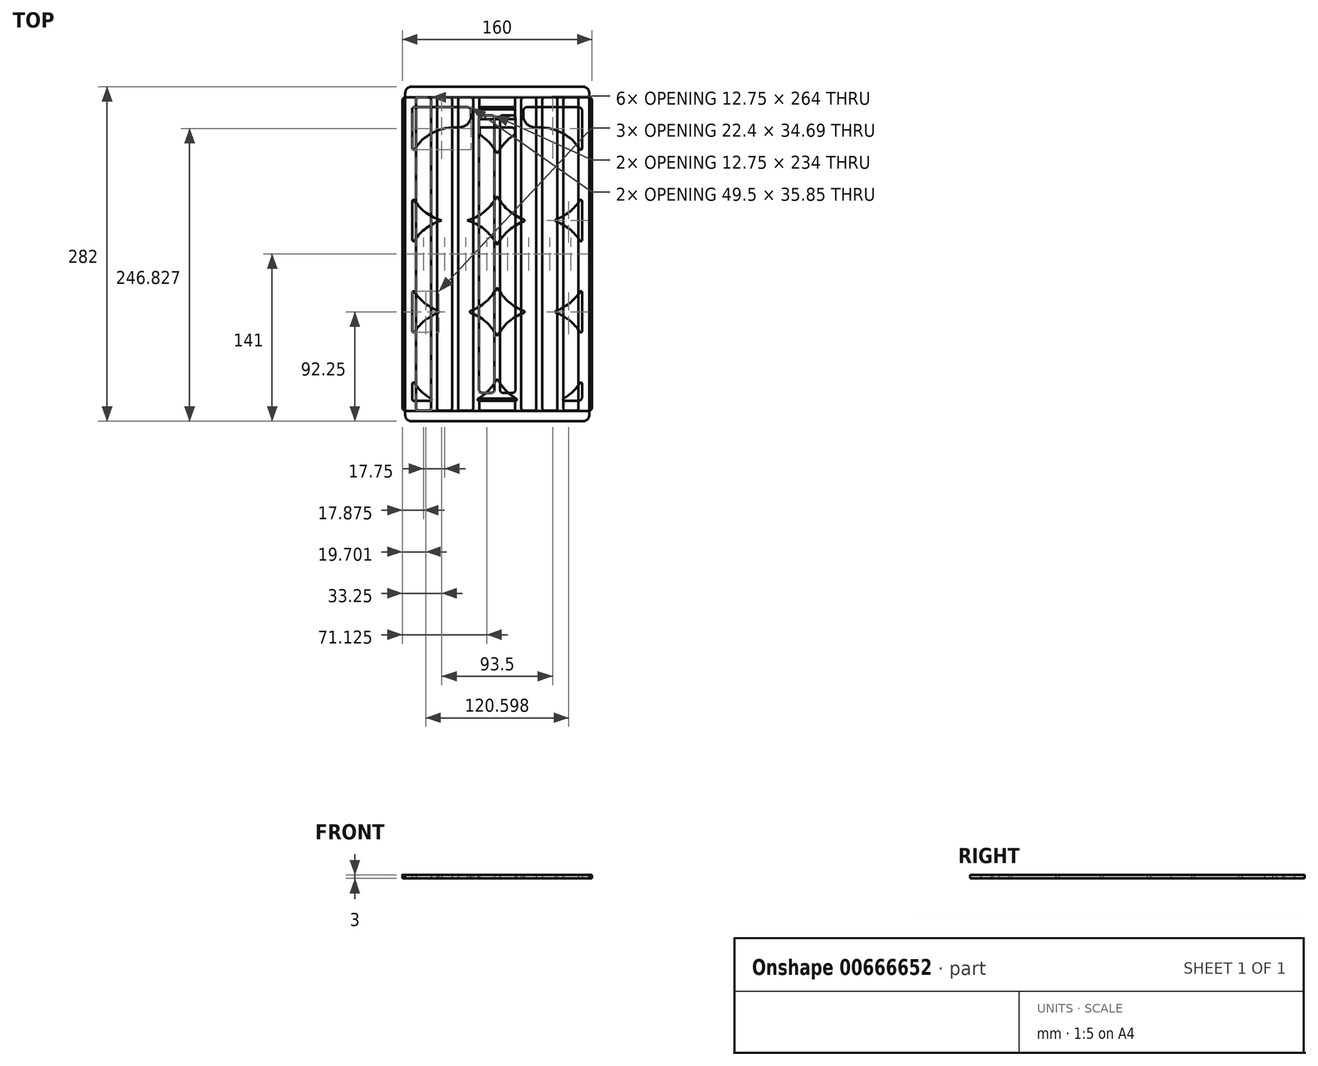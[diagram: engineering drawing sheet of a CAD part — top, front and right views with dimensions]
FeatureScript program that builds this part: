
annotation { "Feature Type Name" : "Feature", "Feature Type Description" : "" }
export const myFeature = defineFeature(function(context is Context, id is Id, definition is map)
    precondition{}
    {
        {
            var Q0;
            Q0=qCreatedBy(makeId("Top.planeOp"),FACE);
            var sketch = newSketch(context, id + "F0", { "sketchPlane" : qUnion([Q0])});
            skLineSegment(sketch, "E0.bottom", {"start": v(-80, 132.25) * mm, "end": v(80, 132.25) * mm});
            skLineSegment(sketch, "E0.top", {"start": v(-80, -132.25) * mm, "end": v(80, -132.25) * mm});
            skLineSegment(sketch, "E0.left", {"start": v(-80, 132.25) * mm, "end": v(-80, -132.25) * mm});
            skLineSegment(sketch, "E0.right", {"start": v(80, 132.25) * mm, "end": v(80, -132.25) * mm});
            skLineSegment(sketch, "E1.0", {"start": v(-71.5, 123.75) * mm, "end": v(-71.5, 85.18) * mm});
            skLineSegment(sketch, "E1.1", {"start": v(-71.5, 123.75) * mm, "end": v(-22, 123.75) * mm});
            skLineSegment(sketch, "E1.2", {"start": v(71.5, 123.75) * mm, "end": v(71.5, 85.18) * mm});
            skLineSegment(sketch, "E1.3", {"start": v(-71.5, -123.75) * mm, "end": v(-52.36, -123.75) * mm});
            skLineSegment(sketch, "E2.bottom", {"start": v(-15, 123.75) * mm, "end": v(15, 123.75) * mm});
            skLineSegment(sketch, "E2.top", {"start": v(-15, 113.75) * mm, "end": v(15, 113.75) * mm});
            skLineSegment(sketch, "E2.left", {"start": v(-15, 123.75) * mm, "end": v(-15, 113.75) * mm});
            skLineSegment(sketch, "E2.right", {"start": v(15, 123.75) * mm, "end": v(15, 113.75) * mm});
            skLineSegment(sketch, "E3", {"start": v(0, 0) * mm, "end": v(0, 132.25) * mm, "construction": true});
            skLineSegment(sketch, "E4", {"start": v(0, 0) * mm, "end": v(71.5, 0) * mm, "construction": true});
            skArc(sketch, "E5", {"start": v(-71.5, -105.68) * mm, "mid": v(-63.46, -116.34) * mm, "end": v(-52.36, -123.75) * mm});
            skArc(sketch, "E6", {"start": v(-71.5, 48.32) * mm, "mid": v(-61.25, 35.73) * mm, "end": v(-46.85, 28.25) * mm});
            skLineSegment(sketch, "E7", {"start": v(-36, -87.25) * mm, "end": v(-36, 66.75) * mm, "construction": true});
            skArc(sketch, "E8", {"start": v(-46.85, 28.25) * mm, "mid": v(-61.25, 20.77) * mm, "end": v(-71.5, 8.18) * mm});
            skArc(sketch, "E9.MirrorC", {"start": v(-25.15, -48.75) * mm, "mid": v(-10.32, -56.59) * mm, "end": v(0, -69.81) * mm});
            skArc(sketch, "E10.MirrorC", {"start": v(-25.15, 28.25) * mm, "mid": v(-10.32, 20.41) * mm, "end": v(0, 7.19) * mm});
            skArc(sketch, "E11.MirrorC", {"start": v(-71.5, 85.18) * mm, "mid": v(-56.77, 100.94) * mm, "end": v(-36, 106.75) * mm});
            skArc(sketch, "E12.MirrorC", {"start": v(0, 49.31) * mm, "mid": v(10.32, 36.09) * mm, "end": v(25.15, 28.25) * mm});
            skArc(sketch, "E13.MirrorC", {"start": v(71.5, -28.68) * mm, "mid": v(61.25, -41.27) * mm, "end": v(46.85, -48.75) * mm});
            skArc(sketch, "E14.MirrorC", {"start": v(52.36, -123.75) * mm, "mid": v(63.46, -116.34) * mm, "end": v(71.5, -105.68) * mm});
            skLineSegment(sketch, "E15.MirrorCS", {"start": v(36, -87.25) * mm, "end": v(36, 66.75) * mm, "construction": true});
            skLineSegment(sketch, "E16.0", {"start": v(22, 123.75) * mm, "end": v(22, 106.75) * mm});
            skLineSegment(sketch, "E16.1", {"start": v(-14.66, 106.75) * mm, "end": v(15.03, 106.75) * mm});
            skLineSegment(sketch, "E16.2", {"start": v(-22, 123.75) * mm, "end": v(-22, 106.75) * mm});
            skLineSegment(sketch, "E17", {"start": v(-22, 106.75) * mm, "end": v(-36, 106.75) * mm});
            skLineSegment(sketch, "E18", {"start": v(-14.66, 106.75) * mm, "end": v(-14.66, 100.58) * mm});
            skLineSegment(sketch, "E19", {"start": v(15.03, 106.75) * mm, "end": v(15.03, 100.82) * mm});
            skLineSegment(sketch, "E20", {"start": v(22, 106.75) * mm, "end": v(36, 106.75) * mm});
            skArc(sketch, "E21.trimOffspring", {"start": v(0, 49.31) * mm, "mid": v(-10.32, 36.09) * mm, "end": v(-25.15, 28.25) * mm});
            skArc(sketch, "E22.trimOffspring", {"start": v(0, 84.19) * mm, "mid": v(-6.18, 93.41) * mm, "end": v(-14.66, 100.58) * mm});
            skLineSegment(sketch, "E23.trimOffspring", {"start": v(71.5, 48.32) * mm, "end": v(71.5, 8.18) * mm});
            skLineSegment(sketch, "E24.trimOffspring", {"start": v(-71.5, 48.32) * mm, "end": v(-71.5, 8.18) * mm});
            skLineSegment(sketch, "E25.trimOffspring", {"start": v(22, 123.75) * mm, "end": v(71.5, 123.75) * mm});
            skArc(sketch, "E26.trimOffspring", {"start": v(15.03, 100.82) * mm, "mid": v(6.33, 93.58) * mm, "end": v(0, 84.19) * mm});
            skArc(sketch, "E27.trimOffspring", {"start": v(-36, 106.75) * mm, "mid": v(-56.77, 100.94) * mm, "end": v(-71.5, 85.18) * mm});
            skArc(sketch, "E28.trimOffspring", {"start": v(-14.66, 100.58) * mm, "mid": v(-6.18, 93.41) * mm, "end": v(0, 84.19) * mm});
            skArc(sketch, "E29.trimOffspring", {"start": v(-46.85, 28.25) * mm, "mid": v(-61.25, 35.73) * mm, "end": v(-71.5, 48.32) * mm});
            skArc(sketch, "E30.trimOffspring", {"start": v(-25.15, 28.25) * mm, "mid": v(-10.32, 36.09) * mm, "end": v(0, 49.31) * mm});
            skArc(sketch, "E31.trimOffspring", {"start": v(-71.5, -28.68) * mm, "mid": v(-61.25, -41.27) * mm, "end": v(-46.85, -48.75) * mm});
            skArc(sketch, "E32.trimOffspring", {"start": v(-71.5, 8.18) * mm, "mid": v(-61.25, 20.77) * mm, "end": v(-46.85, 28.25) * mm});
            skLineSegment(sketch, "E33.trimOffspring", {"start": v(-71.5, -28.68) * mm, "end": v(-71.5, -68.82) * mm});
            skLineSegment(sketch, "E34.trimOffspring", {"start": v(71.5, -28.68) * mm, "end": v(71.5, -68.82) * mm});
            skArc(sketch, "E35.trimOffspring", {"start": v(0, -27.69) * mm, "mid": v(-10.32, -40.91) * mm, "end": v(-25.15, -48.75) * mm});
            skArc(sketch, "E36.trimOffspring", {"start": v(0, 7.19) * mm, "mid": v(-10.32, 20.41) * mm, "end": v(-25.15, 28.25) * mm});
            skArc(sketch, "E37.trimOffspring", {"start": v(0, 7.19) * mm, "mid": v(10.32, 20.41) * mm, "end": v(25.15, 28.25) * mm});
            skArc(sketch, "E38.trimOffspring", {"start": v(-46.85, -48.75) * mm, "mid": v(-61.25, -41.27) * mm, "end": v(-71.5, -28.68) * mm});
            skArc(sketch, "E39.trimOffspring", {"start": v(-25.15, -48.75) * mm, "mid": v(-10.32, -40.91) * mm, "end": v(0, -27.69) * mm});
            skArc(sketch, "E40.trimOffspring", {"start": v(-71.5, -68.82) * mm, "mid": v(-61.25, -56.23) * mm, "end": v(-46.85, -48.75) * mm});
            skLineSegment(sketch, "E41.trimOffspring", {"start": v(-71.5, -105.68) * mm, "end": v(-71.5, -123.75) * mm});
            skArc(sketch, "E42.trimOffspring", {"start": v(-52.36, -123.75) * mm, "mid": v(-63.46, -116.34) * mm, "end": v(-71.5, -105.68) * mm});
            skArc(sketch, "E43.trimOffspring", {"start": v(-19.64, -123.75) * mm, "mid": v(-8.14, -115.95) * mm, "end": v(0, -104.69) * mm});
            skLineSegment(sketch, "E44.trimOffspring", {"start": v(-19.64, -123.75) * mm, "end": v(19.64, -123.75) * mm});
            skLineSegment(sketch, "E45.trimOffspring", {"start": v(52.36, -123.75) * mm, "end": v(71.5, -123.75) * mm});
            skArc(sketch, "E46.trimOffspring", {"start": v(25.15, -48.75) * mm, "mid": v(10.32, -56.59) * mm, "end": v(0, -69.81) * mm});
            skArc(sketch, "E47.trimOffspring", {"start": v(25.15, -48.75) * mm, "mid": v(10.32, -40.91) * mm, "end": v(0, -27.69) * mm});
            skArc(sketch, "E48.trimOffspring", {"start": v(71.5, -68.82) * mm, "mid": v(61.25, -56.23) * mm, "end": v(46.85, -48.75) * mm});
            skLineSegment(sketch, "E49.trimOffspring", {"start": v(71.5, -105.68) * mm, "end": v(71.5, -123.75) * mm});
            skArc(sketch, "E50.trimOffspring", {"start": v(0, -104.69) * mm, "mid": v(-8.14, -115.95) * mm, "end": v(-19.64, -123.75) * mm});
            skArc(sketch, "E51.trimOffspring", {"start": v(0, -104.69) * mm, "mid": v(8.14, -115.95) * mm, "end": v(19.64, -123.75) * mm});
            skArc(sketch, "E52.trimOffspring", {"start": v(46.85, 28.25) * mm, "mid": v(61.25, 20.77) * mm, "end": v(71.5, 8.18) * mm});
            skArc(sketch, "E53.trimOffspring", {"start": v(46.85, 28.25) * mm, "mid": v(61.25, 35.73) * mm, "end": v(71.5, 48.32) * mm});
            skArc(sketch, "E54", {"start": v(36, 106.75) * mm, "mid": v(56.77, 100.94) * mm, "end": v(71.5, 85.18) * mm});
            skSolve(sketch);
        }
        {
            var Q0;
            Q0=makeQuery(id+"F0.imprint","IMPRINT",FACE,{"disambiguationData":[TD([[makeQuery(id+"F0.imprint","IMPRINT",EDGE,{"derivedFrom":sQuery(id+"F0.wireOp",EDGE,"E0.bottom")}),-1.0]])]});
            extrude(context, id + "F1", {"entities" : qUnion([Q0]), "depth" : 3 * mm, "offsetDistance" : 25 * mm});
        }
        {
            var Q0;
            Q0=makeQuery(id+"F1.opExtrude","SWEPT_EDGE",EDGE,{"disambiguationData":[OSD([sQuery(id+"F0.wireOp",EDGE,"E16.0"),sQuery(id+"F0.wireOp",EDGE,"E20")])]});
            var Q1;
            Q1=makeQuery(id+"F1.opExtrude","SWEPT_EDGE",EDGE,{"disambiguationData":[OSD([sQuery(id+"F0.wireOp",EDGE,"E16.2"),sQuery(id+"F0.wireOp",EDGE,"E17")])]});
            fillet(context, id + "F2", {"entities" : qUnion([Q0, Q1]), "radius" : 10 * mm, "tangentPropagation" : true, "allowEdgeOverflow" : false});
        }
        {
            var Q0;
            Q0=makeQuery(id+"F1.opExtrude","SWEPT_EDGE",EDGE,{"disambiguationData":[OSD([sQuery(id+"F0.wireOp",EDGE,"E36.trimOffspring"),sQuery(id+"F0.wireOp",EDGE,"E37.trimOffspring")])]});
            var Q1;
            Q1=makeQuery(id+"F1.opExtrude","SWEPT_EDGE",EDGE,{"disambiguationData":[OSD([sQuery(id+"F0.wireOp",EDGE,"E26.trimOffspring"),sQuery(id+"F0.wireOp",EDGE,"E28.trimOffspring")])]});
            var Q2;
            Q2=makeQuery(id+"F1.opExtrude","SWEPT_EDGE",EDGE,{"disambiguationData":[OSD([sQuery(id+"F0.wireOp",EDGE,"E12.MirrorC"),sQuery(id+"F0.wireOp",EDGE,"E37.trimOffspring")])]});
            var Q3;
            Q3=makeQuery(id+"F1.opExtrude","SWEPT_EDGE",EDGE,{"disambiguationData":[OSD([sQuery(id+"F0.wireOp",EDGE,"E29.trimOffspring"),sQuery(id+"F0.wireOp",EDGE,"E32.trimOffspring")])]});
            var Q4;
            Q4=makeQuery(id+"F1.opExtrude","SWEPT_EDGE",EDGE,{"disambiguationData":[OSD([sQuery(id+"F0.wireOp",EDGE,"E19"),sQuery(id+"F0.wireOp",EDGE,"E26.trimOffspring")])]});
            var Q5;
            Q5=makeQuery(id+"F1.opExtrude","SWEPT_EDGE",EDGE,{"disambiguationData":[OSD([sQuery(id+"F0.wireOp",EDGE,"E18"),sQuery(id+"F0.wireOp",EDGE,"E28.trimOffspring")])]});
            var Q6;
            Q6=makeQuery(id+"F1.opExtrude","SWEPT_EDGE",EDGE,{"disambiguationData":[OSD([sQuery(id+"F0.wireOp",EDGE,"E30.trimOffspring"),sQuery(id+"F0.wireOp",EDGE,"E36.trimOffspring")])]});
            var Q7;
            Q7=makeQuery(id+"F1.opExtrude","SWEPT_EDGE",EDGE,{"disambiguationData":[OSD([sQuery(id+"F0.wireOp",EDGE,"E12.MirrorC"),sQuery(id+"F0.wireOp",EDGE,"E30.trimOffspring")])]});
            var Q8;
            Q8=makeQuery(id+"F1.opExtrude","SWEPT_EDGE",EDGE,{"disambiguationData":[OSD([sQuery(id+"F0.wireOp",EDGE,"E52.trimOffspring"),sQuery(id+"F0.wireOp",EDGE,"E53.trimOffspring")])]});
            var Q9;
            Q9=makeQuery(id+"F1.opExtrude","SWEPT_EDGE",EDGE,{"disambiguationData":[OSD([sQuery(id+"F0.wireOp",EDGE,"E23.trimOffspring"),sQuery(id+"F0.wireOp",EDGE,"E52.trimOffspring")])]});
            var Q10;
            Q10=makeQuery(id+"F1.opExtrude","SWEPT_EDGE",EDGE,{"disambiguationData":[OSD([sQuery(id+"F0.wireOp",EDGE,"E1.2"),sQuery(id+"F0.wireOp",EDGE,"E54")])]});
            var Q11;
            Q11=makeQuery(id+"F1.opExtrude","SWEPT_EDGE",EDGE,{"disambiguationData":[OSD([sQuery(id+"F0.wireOp",EDGE,"E9.MirrorC"),sQuery(id+"F0.wireOp",EDGE,"E46.trimOffspring")])]});
            var Q12;
            Q12=makeQuery(id+"F1.opExtrude","SWEPT_EDGE",EDGE,{"disambiguationData":[OSD([sQuery(id+"F0.wireOp",EDGE,"E9.MirrorC"),sQuery(id+"F0.wireOp",EDGE,"E39.trimOffspring")])]});
            var Q13;
            Q13=makeQuery(id+"F1.opExtrude","SWEPT_EDGE",EDGE,{"disambiguationData":[OSD([sQuery(id+"F0.wireOp",EDGE,"E39.trimOffspring"),sQuery(id+"F0.wireOp",EDGE,"E47.trimOffspring")])]});
            var Q14;
            Q14=makeQuery(id+"F1.opExtrude","SWEPT_EDGE",EDGE,{"disambiguationData":[OSD([sQuery(id+"F0.wireOp",EDGE,"E46.trimOffspring"),sQuery(id+"F0.wireOp",EDGE,"E47.trimOffspring")])]});
            var Q15;
            Q15=makeQuery(id+"F1.opExtrude","SWEPT_EDGE",EDGE,{"disambiguationData":[OSD([sQuery(id+"F0.wireOp",EDGE,"E13.MirrorC"),sQuery(id+"F0.wireOp",EDGE,"E34.trimOffspring")])]});
            var Q16;
            Q16=makeQuery(id+"F1.opExtrude","SWEPT_EDGE",EDGE,{"disambiguationData":[OSD([sQuery(id+"F0.wireOp",EDGE,"E13.MirrorC"),sQuery(id+"F0.wireOp",EDGE,"E48.trimOffspring")])]});
            var Q17;
            Q17=makeQuery(id+"F1.opExtrude","SWEPT_EDGE",EDGE,{"disambiguationData":[OSD([sQuery(id+"F0.wireOp",EDGE,"E34.trimOffspring"),sQuery(id+"F0.wireOp",EDGE,"E48.trimOffspring")])]});
            var Q18;
            Q18=makeQuery(id+"F1.opExtrude","SWEPT_EDGE",EDGE,{"disambiguationData":[OSD([sQuery(id+"F0.wireOp",EDGE,"E38.trimOffspring"),sQuery(id+"F0.wireOp",EDGE,"E40.trimOffspring")])]});
            var Q19;
            Q19=makeQuery(id+"F1.opExtrude","SWEPT_EDGE",EDGE,{"disambiguationData":[OSD([sQuery(id+"F0.wireOp",EDGE,"E33.trimOffspring"),sQuery(id+"F0.wireOp",EDGE,"E40.trimOffspring")])]});
            var Q20;
            Q20=makeQuery(id+"F1.opExtrude","SWEPT_EDGE",EDGE,{"disambiguationData":[OSD([sQuery(id+"F0.wireOp",EDGE,"E33.trimOffspring"),sQuery(id+"F0.wireOp",EDGE,"E38.trimOffspring")])]});
            var Q21;
            Q21=makeQuery(id+"F1.opExtrude","SWEPT_EDGE",EDGE,{"disambiguationData":[OSD([sQuery(id+"F0.wireOp",EDGE,"E24.trimOffspring"),sQuery(id+"F0.wireOp",EDGE,"E29.trimOffspring")])]});
            var Q22;
            Q22=makeQuery(id+"F1.opExtrude","SWEPT_EDGE",EDGE,{"disambiguationData":[OSD([sQuery(id+"F0.wireOp",EDGE,"E41.trimOffspring"),sQuery(id+"F0.wireOp",EDGE,"E42.trimOffspring")])]});
            var Q23;
            Q23=makeQuery(id+"F1.opExtrude","SWEPT_EDGE",EDGE,{"disambiguationData":[OSD([sQuery(id+"F0.wireOp",EDGE,"E1.3"),sQuery(id+"F0.wireOp",EDGE,"E42.trimOffspring")])]});
            var Q24;
            Q24=makeQuery(id+"F1.opExtrude","SWEPT_EDGE",EDGE,{"disambiguationData":[OSD([sQuery(id+"F0.wireOp",EDGE,"E44.trimOffspring"),sQuery(id+"F0.wireOp",EDGE,"E50.trimOffspring")])]});
            var Q25;
            Q25=makeQuery(id+"F1.opExtrude","SWEPT_EDGE",EDGE,{"disambiguationData":[OSD([sQuery(id+"F0.wireOp",EDGE,"E50.trimOffspring"),sQuery(id+"F0.wireOp",EDGE,"E51.trimOffspring")])]});
            var Q26;
            Q26=makeQuery(id+"F1.opExtrude","SWEPT_EDGE",EDGE,{"disambiguationData":[OSD([sQuery(id+"F0.wireOp",EDGE,"E44.trimOffspring"),sQuery(id+"F0.wireOp",EDGE,"E51.trimOffspring")])]});
            var Q27;
            Q27=makeQuery(id+"F1.opExtrude","SWEPT_EDGE",EDGE,{"disambiguationData":[OSD([sQuery(id+"F0.wireOp",EDGE,"E14.MirrorC"),sQuery(id+"F0.wireOp",EDGE,"E45.trimOffspring")])]});
            var Q28;
            Q28=makeQuery(id+"F1.opExtrude","SWEPT_EDGE",EDGE,{"disambiguationData":[OSD([sQuery(id+"F0.wireOp",EDGE,"E14.MirrorC"),sQuery(id+"F0.wireOp",EDGE,"E49.trimOffspring")])]});
            var Q29;
            Q29=makeQuery(id+"F1.opExtrude","SWEPT_EDGE",EDGE,{"disambiguationData":[OSD([sQuery(id+"F0.wireOp",EDGE,"E23.trimOffspring"),sQuery(id+"F0.wireOp",EDGE,"E53.trimOffspring")])]});
            var Q30;
            Q30=makeQuery(id+"F1.opExtrude","SWEPT_EDGE",EDGE,{"disambiguationData":[OSD([sQuery(id+"F0.wireOp",EDGE,"E24.trimOffspring"),sQuery(id+"F0.wireOp",EDGE,"E32.trimOffspring")])]});
            var Q31;
            Q31=makeQuery(id+"F1.opExtrude","SWEPT_EDGE",EDGE,{"disambiguationData":[OSD([sQuery(id+"F0.wireOp",EDGE,"E1.0"),sQuery(id+"F0.wireOp",EDGE,"E27.trimOffspring")])]});
            fillet(context, id + "F3", {"entities" : qUnion([Q0, Q1, Q2, Q3, Q4, Q5, Q6, Q7, Q8, Q9, Q10, Q11, Q12, Q13, Q14, Q15, Q16, Q17, Q18, Q19, Q20, Q21, Q22, Q23, Q24, Q25, Q26, Q27, Q28, Q29, Q30, Q31]), "radius" : 1 * mm, "tangentPropagation" : true, "defaultsChanged" : false, "vertexSettings" : [], "allowEdgeOverflow" : false});
        }
        {
            var Q0;
            Q0=makeQuery(id+"F1.opExtrude","SWEPT_EDGE",EDGE,{"disambiguationData":[OSD([sQuery(id+"F0.wireOp",EDGE,"E1.0"),sQuery(id+"F0.wireOp",EDGE,"E1.1")])]});
            var Q1;
            Q1=makeQuery(id+"F1.opExtrude","SWEPT_EDGE",EDGE,{"disambiguationData":[OSD([sQuery(id+"F0.wireOp",EDGE,"E1.1"),sQuery(id+"F0.wireOp",EDGE,"E16.2")])]});
            var Q2;
            Q2=makeQuery(id+"F1.opExtrude","SWEPT_EDGE",EDGE,{"disambiguationData":[OSD([sQuery(id+"F0.wireOp",EDGE,"E16.1"),sQuery(id+"F0.wireOp",EDGE,"E18")])]});
            var Q3;
            Q3=makeQuery(id+"F1.opExtrude","SWEPT_EDGE",EDGE,{"disambiguationData":[OSD([sQuery(id+"F0.wireOp",EDGE,"E16.1"),sQuery(id+"F0.wireOp",EDGE,"E19")])]});
            var Q4;
            Q4=makeQuery(id+"F1.opExtrude","SWEPT_EDGE",EDGE,{"disambiguationData":[OSD([sQuery(id+"F0.wireOp",EDGE,"E16.0"),sQuery(id+"F0.wireOp",EDGE,"E25.trimOffspring")])]});
            var Q5;
            Q5=makeQuery(id+"F1.opExtrude","SWEPT_EDGE",EDGE,{"disambiguationData":[OSD([sQuery(id+"F0.wireOp",EDGE,"E1.2"),sQuery(id+"F0.wireOp",EDGE,"E25.trimOffspring")])]});
            var Q6;
            Q6=makeQuery(id+"F1.opExtrude","SWEPT_EDGE",EDGE,{"disambiguationData":[OSD([sQuery(id+"F0.wireOp",EDGE,"E1.3"),sQuery(id+"F0.wireOp",EDGE,"E41.trimOffspring")])]});
            var Q7;
            Q7=makeQuery(id+"F1.opExtrude","SWEPT_EDGE",EDGE,{"disambiguationData":[OSD([sQuery(id+"F0.wireOp",EDGE,"E45.trimOffspring"),sQuery(id+"F0.wireOp",EDGE,"E49.trimOffspring")])]});
            var Q8;
            Q8=makeQuery(id+"F1.opExtrude","SWEPT_EDGE",EDGE,{"disambiguationData":[OSD([sQuery(id+"F0.wireOp",EDGE,"E0.bottom"),sQuery(id+"F0.wireOp",EDGE,"E0.right")])]});
            var Q9;
            Q9=makeQuery(id+"F1.opExtrude","SWEPT_EDGE",EDGE,{"disambiguationData":[OSD([sQuery(id+"F0.wireOp",EDGE,"E0.top"),sQuery(id+"F0.wireOp",EDGE,"E0.right")])]});
            var Q10;
            Q10=makeQuery(id+"F1.opExtrude","SWEPT_EDGE",EDGE,{"disambiguationData":[OSD([sQuery(id+"F0.wireOp",EDGE,"E0.top"),sQuery(id+"F0.wireOp",EDGE,"E0.left")])]});
            var Q11;
            Q11=makeQuery(id+"F1.opExtrude","SWEPT_EDGE",EDGE,{"disambiguationData":[OSD([sQuery(id+"F0.wireOp",EDGE,"E0.bottom"),sQuery(id+"F0.wireOp",EDGE,"E0.left")])]});
            fillet(context, id + "F4", {"entities" : qUnion([Q0, Q1, Q2, Q3, Q4, Q5, Q6, Q7, Q8, Q9, Q10, Q11]), "radius" : 3 * mm, "tangentPropagation" : true, "defaultsChanged" : false, "vertexSettings" : [], "allowEdgeOverflow" : false});
        }
        {
            var Q0;
            Q0=makeQuery(id+"F1.opExtrude","SWEPT_EDGE",EDGE,{"disambiguationData":[OSD([sQuery(id+"F0.wireOp",EDGE,"E2.top"),sQuery(id+"F0.wireOp",EDGE,"E2.right")])]});
            var Q1;
            Q1=makeQuery(id+"F1.opExtrude","SWEPT_EDGE",EDGE,{"disambiguationData":[OSD([sQuery(id+"F0.wireOp",EDGE,"E2.top"),sQuery(id+"F0.wireOp",EDGE,"E2.left")])]});
            var Q2;
            Q2=makeQuery(id+"F1.opExtrude","SWEPT_EDGE",EDGE,{"disambiguationData":[OSD([sQuery(id+"F0.wireOp",EDGE,"E2.bottom"),sQuery(id+"F0.wireOp",EDGE,"E2.left")])]});
            var Q3;
            Q3=makeQuery(id+"F1.opExtrude","SWEPT_EDGE",EDGE,{"disambiguationData":[OSD([sQuery(id+"F0.wireOp",EDGE,"E2.bottom"),sQuery(id+"F0.wireOp",EDGE,"E2.right")])]});
            fillet(context, id + "F5", {"entities" : qUnion([Q0, Q1, Q2, Q3]), "radius" : 0.5 * mm, "tangentPropagation" : true, "allowEdgeOverflow" : false});
        }
        {
            var Q0;
            Q0=qCreatedBy(makeId("Top.planeOp"),FACE);
            var sketch = newSketch(context, id + "F6", { "sketchPlane" : qUnion([Q0])});
            skLineSegment(sketch, "E55.0", {"start": v(-77.5, 141) * mm, "end": v(-77.5, -141) * mm});
            skLineSegment(sketch, "E55.1", {"start": v(-77.5, 141) * mm, "end": v(77.5, 141) * mm});
            skLineSegment(sketch, "E55.2", {"start": v(77.5, 141) * mm, "end": v(77.5, -141) * mm});
            skLineSegment(sketch, "E55.3", {"start": v(-77.5, -141) * mm, "end": v(77.5, -141) * mm});
            skLineSegment(sketch, "E56.1", {"start": v(-68.5, 132) * mm, "end": v(-55.75, 132) * mm});
            skLineSegment(sketch, "E56.2", {"start": v(-15, 132) * mm, "end": v(15, 132) * mm});
            skLineSegment(sketch, "E56.5", {"start": v(-15, 132) * mm, "end": v(-15, 122) * mm});
            skLineSegment(sketch, "E56.6", {"start": v(-15, 122) * mm, "end": v(15, 122) * mm});
            skLineSegment(sketch, "E56.7", {"start": v(15, 132) * mm, "end": v(15, 122) * mm});
            skLineSegment(sketch, "E56.8", {"start": v(-15.25, 117) * mm, "end": v(-2.5, 117) * mm});
            skPoint(sketch, "E57.0", {"position": v(-68.5, -132) * mm});
            skPoint(sketch, "E57.1", {"position": v(68.5, -132) * mm});
            skLineSegment(sketch, "E58", {"start": v(-68.5, 132) * mm, "end": v(-68.5, -132) * mm});
            skLineSegment(sketch, "E59", {"start": v(-68.5, -132) * mm, "end": v(-55.75, -132) * mm});
            skLineSegment(sketch, "E60", {"start": v(-55.75, 132) * mm, "end": v(-55.75, -132) * mm});
            skLineSegment(sketch, "E61", {"start": v(-50.75, 132) * mm, "end": v(-50.75, -132) * mm});
            skLineSegment(sketch, "E62.1.0.0", {"start": v(-38, 132) * mm, "end": v(-38, -132) * mm});
            skLineSegment(sketch, "E62.1.0.1", {"start": v(-33, 132) * mm, "end": v(-33, -132) * mm});
            skLineSegment(sketch, "E62.2.0.0", {"start": v(-20.25, 132) * mm, "end": v(-20.25, -132) * mm});
            skLineSegment(sketch, "E62.2.0.1", {"start": v(-15.25, 117) * mm, "end": v(-15.25, -117) * mm});
            skLineSegment(sketch, "E62.3.0.0", {"start": v(-2.5, 117) * mm, "end": v(-2.5, -117) * mm});
            skLineSegment(sketch, "E62.5.0.0", {"start": v(15.25, 117) * mm, "end": v(15.25, -117) * mm});
            skLineSegment(sketch, "E62.5.0.1", {"start": v(20.25, 132) * mm, "end": v(20.25, -132) * mm});
            skLineSegment(sketch, "E62.6.0.0", {"start": v(33, 132) * mm, "end": v(33, -132) * mm});
            skLineSegment(sketch, "E62.6.0.1", {"start": v(38, 132) * mm, "end": v(38, -132) * mm});
            skLineSegment(sketch, "E62.7.0.0", {"start": v(50.75, 132) * mm, "end": v(50.75, -132) * mm});
            skLineSegment(sketch, "E62.7.0.1", {"start": v(55.75, 132) * mm, "end": v(55.75, -132) * mm});
            skLineSegment(sketch, "E62.8.0.0", {"start": v(68.5, 132) * mm, "end": v(68.5, -132) * mm});
            skLineSegment(sketch, "E62.direction1", {"start": v(-50.75, -132) * mm, "end": v(-38, -132) * mm, "construction": true});
            skLineSegment(sketch, "E63.trimOffspring", {"start": v(-50.75, 132) * mm, "end": v(-38, 132) * mm});
            skLineSegment(sketch, "E64.trimOffspring", {"start": v(-33, 132) * mm, "end": v(-20.25, 132) * mm});
            skLineSegment(sketch, "E65.trimOffspring", {"start": v(2.5, 117) * mm, "end": v(2.5, -117) * mm});
            skLineSegment(sketch, "E66.trimOffspring", {"start": v(20.25, 132) * mm, "end": v(33, 132) * mm});
            skLineSegment(sketch, "E67.trimOffspring", {"start": v(38, 132) * mm, "end": v(50.75, 132) * mm});
            skLineSegment(sketch, "E68.trimOffspring", {"start": v(55.75, 132) * mm, "end": v(68.5, 132) * mm});
            skLineSegment(sketch, "E69.trimOffspring", {"start": v(2.5, 117) * mm, "end": v(15.25, 117) * mm});
            skLineSegment(sketch, "E70.trimOffspring", {"start": v(-50.75, -132) * mm, "end": v(-38, -132) * mm});
            skLineSegment(sketch, "E71.trimOffspring", {"start": v(-33, -132) * mm, "end": v(-20.25, -132) * mm});
            skLineSegment(sketch, "E72.trimOffspring", {"start": v(-15, -132) * mm, "end": v(15, -132) * mm});
            skLineSegment(sketch, "E73.trimOffspring", {"start": v(20.25, -132) * mm, "end": v(33, -132) * mm});
            skLineSegment(sketch, "E74.trimOffspring", {"start": v(38, -132) * mm, "end": v(50.75, -132) * mm});
            skLineSegment(sketch, "E75.trimOffspring", {"start": v(55.75, -132) * mm, "end": v(68.5, -132) * mm});
            skLineSegment(sketch, "E76", {"start": v(0, 0) * mm, "end": v(0, 26.47) * mm, "construction": true});
            skLineSegment(sketch, "E77", {"start": v(-55.75, -132) * mm, "end": v(-50.75, -132) * mm, "construction": true});
            skLineSegment(sketch, "E78", {"start": v(-38, -132) * mm, "end": v(-33, -132) * mm, "construction": true});
            skLineSegment(sketch, "E79", {"start": v(33, -132) * mm, "end": v(38, -132) * mm, "construction": true});
            skLineSegment(sketch, "E80", {"start": v(50.75, -132) * mm, "end": v(55.75, -132) * mm, "construction": true});
            skLineSegment(sketch, "E81", {"start": v(0, 0) * mm, "end": v(104.79, 0) * mm, "construction": true});
            skLineSegment(sketch, "E82.MirrorCS", {"start": v(15, -132) * mm, "end": v(15, -122) * mm});
            skLineSegment(sketch, "E83.MirrorCS", {"start": v(-15, -122) * mm, "end": v(15, -122) * mm});
            skLineSegment(sketch, "E84.MirrorCS", {"start": v(-15, -132) * mm, "end": v(-15, -122) * mm});
            skPoint(sketch, "E85.trimOffspring.end.orphan", {"position": v(15, -132) * mm});
            skLineSegment(sketch, "E86.MirrorCS", {"start": v(2.5, -117) * mm, "end": v(15.25, -117) * mm});
            skLineSegment(sketch, "E87.MirrorCS", {"start": v(-15.25, -117) * mm, "end": v(-2.5, -117) * mm});
            skPoint(sketch, "E88.MirrorCS.start.orphan", {"position": v(-15, -132) * mm});
            skLineSegment(sketch, "E89", {"start": v(-15.25, -117) * mm, "end": v(-20.25, -117) * mm, "construction": true});
            skLineSegment(sketch, "E90", {"start": v(15.25, -117) * mm, "end": v(20.25, -117) * mm, "construction": true});
            skLineSegment(sketch, "E91", {"start": v(-2.5, -117) * mm, "end": v(2.5, -117) * mm, "construction": true});
            skSolve(sketch);
        }
        {
            var Q0;
            Q0=makeQuery(id+"F6.imprint","IMPRINT",FACE,{"disambiguationData":[TD([[makeQuery(id+"F6.imprint","IMPRINT",EDGE,{"derivedFrom":sQuery(id+"F6.wireOp",EDGE,"E55.0")}),1.0]])]});
            extrude(context, id + "F7", {"entities" : qUnion([Q0]), "depth" : 3 * mm, "offsetDistance" : 25 * mm});
        }
        {
            var Q0;
            Q0=makeQuery(id+"F7.opExtrude","SWEPT_EDGE",EDGE,{"disambiguationData":[OSD([sQuery(id+"F6.wireOp",EDGE,"E55.1"),sQuery(id+"F6.wireOp",EDGE,"E55.2")])]});
            var Q1;
            Q1=makeQuery(id+"F7.opExtrude","SWEPT_EDGE",EDGE,{"disambiguationData":[OSD([sQuery(id+"F6.wireOp",EDGE,"E55.2"),sQuery(id+"F6.wireOp",EDGE,"E55.3")])]});
            var Q2;
            Q2=makeQuery(id+"F7.opExtrude","SWEPT_EDGE",EDGE,{"disambiguationData":[OSD([sQuery(id+"F6.wireOp",EDGE,"E55.0"),sQuery(id+"F6.wireOp",EDGE,"E55.3")])]});
            var Q3;
            Q3=makeQuery(id+"F7.opExtrude","SWEPT_EDGE",EDGE,{"disambiguationData":[OSD([sQuery(id+"F6.wireOp",EDGE,"E55.0"),sQuery(id+"F6.wireOp",EDGE,"E55.1")])]});
            fillet(context, id + "F8", {"entities" : qUnion([Q0, Q1, Q2, Q3]), "tangentPropagation" : true, "radius" : 5 * mm, "defaultsChanged" : true, "vertexSettings" : [], "allowEdgeOverflow" : false});
        }
        {
            var Q0;
            Q0=makeQuery(id+"F7.opExtrude","SWEPT_EDGE",EDGE,{"disambiguationData":[OSD([sQuery(id+"F6.wireOp",EDGE,"E56.1"),sQuery(id+"F6.wireOp",EDGE,"E58")])]});
            var Q1;
            Q1=makeQuery(id+"F7.opExtrude","SWEPT_EDGE",EDGE,{"disambiguationData":[OSD([sQuery(id+"F6.wireOp",EDGE,"E56.1"),sQuery(id+"F6.wireOp",EDGE,"E60")])]});
            var Q2;
            Q2=makeQuery(id+"F7.opExtrude","SWEPT_EDGE",EDGE,{"disambiguationData":[OSD([sQuery(id+"F6.wireOp",EDGE,"E61"),sQuery(id+"F6.wireOp",EDGE,"E63.trimOffspring")])]});
            var Q3;
            Q3=makeQuery(id+"F7.opExtrude","SWEPT_EDGE",EDGE,{"disambiguationData":[OSD([sQuery(id+"F6.wireOp",EDGE,"E62.1.0.0"),sQuery(id+"F6.wireOp",EDGE,"E63.trimOffspring")])]});
            var Q4;
            Q4=makeQuery(id+"F7.opExtrude","SWEPT_EDGE",EDGE,{"disambiguationData":[OSD([sQuery(id+"F6.wireOp",EDGE,"E62.1.0.1"),sQuery(id+"F6.wireOp",EDGE,"E64.trimOffspring")])]});
            var Q5;
            Q5=makeQuery(id+"F7.opExtrude","SWEPT_EDGE",EDGE,{"disambiguationData":[OSD([sQuery(id+"F6.wireOp",EDGE,"E62.2.0.0"),sQuery(id+"F6.wireOp",EDGE,"E64.trimOffspring")])]});
            var Q6;
            Q6=makeQuery(id+"F7.opExtrude","SWEPT_EDGE",EDGE,{"disambiguationData":[OSD([sQuery(id+"F6.wireOp",EDGE,"E56.8"),sQuery(id+"F6.wireOp",EDGE,"E62.2.0.1")])]});
            var Q7;
            Q7=makeQuery(id+"F7.opExtrude","SWEPT_EDGE",EDGE,{"disambiguationData":[OSD([sQuery(id+"F6.wireOp",EDGE,"E56.8"),sQuery(id+"F6.wireOp",EDGE,"E62.3.0.0")])]});
            var Q8;
            Q8=makeQuery(id+"F7.opExtrude","SWEPT_EDGE",EDGE,{"disambiguationData":[OSD([sQuery(id+"F6.wireOp",EDGE,"E62.3.0.1"),sQuery(id+"F6.wireOp",EDGE,"2ed2e225-4777-43f7-924f-b862aec3fb8f.trimOffspring")])]});
            var Q9;
            Q9=makeQuery(id+"F7.opExtrude","SWEPT_EDGE",EDGE,{"disambiguationData":[OSD([sQuery(id+"F6.wireOp",EDGE,"189e8fec-66c5-48d0-8221-c3fc3ef3f735.trimOffspring"),sQuery(id+"F6.wireOp",EDGE,"2ed2e225-4777-43f7-924f-b862aec3fb8f.trimOffspring")])]});
            var Q10;
            Q10=makeQuery(id+"F7.opExtrude","SWEPT_EDGE",EDGE,{"disambiguationData":[OSD([sQuery(id+"F6.wireOp",EDGE,"E65.trimOffspring"),sQuery(id+"F6.wireOp",EDGE,"E69.trimOffspring")])]});
            var Q11;
            Q11=makeQuery(id+"F7.opExtrude","SWEPT_EDGE",EDGE,{"disambiguationData":[OSD([sQuery(id+"F6.wireOp",EDGE,"E62.5.0.0"),sQuery(id+"F6.wireOp",EDGE,"E69.trimOffspring")])]});
            var Q12;
            Q12=makeQuery(id+"F7.opExtrude","SWEPT_EDGE",EDGE,{"disambiguationData":[OSD([sQuery(id+"F6.wireOp",EDGE,"E62.5.0.1"),sQuery(id+"F6.wireOp",EDGE,"E66.trimOffspring")])]});
            var Q13;
            Q13=makeQuery(id+"F7.opExtrude","SWEPT_EDGE",EDGE,{"disambiguationData":[OSD([sQuery(id+"F6.wireOp",EDGE,"E62.6.0.0"),sQuery(id+"F6.wireOp",EDGE,"E66.trimOffspring")])]});
            var Q14;
            Q14=makeQuery(id+"F7.opExtrude","SWEPT_EDGE",EDGE,{"disambiguationData":[OSD([sQuery(id+"F6.wireOp",EDGE,"E62.6.0.1"),sQuery(id+"F6.wireOp",EDGE,"E67.trimOffspring")])]});
            var Q15;
            Q15=makeQuery(id+"F7.opExtrude","SWEPT_EDGE",EDGE,{"disambiguationData":[OSD([sQuery(id+"F6.wireOp",EDGE,"E62.7.0.0"),sQuery(id+"F6.wireOp",EDGE,"E67.trimOffspring")])]});
            var Q16;
            Q16=makeQuery(id+"F7.opExtrude","SWEPT_EDGE",EDGE,{"disambiguationData":[OSD([sQuery(id+"F6.wireOp",EDGE,"E62.7.0.1"),sQuery(id+"F6.wireOp",EDGE,"E68.trimOffspring")])]});
            var Q17;
            Q17=makeQuery(id+"F7.opExtrude","SWEPT_EDGE",EDGE,{"disambiguationData":[OSD([sQuery(id+"F6.wireOp",EDGE,"E62.8.0.0"),sQuery(id+"F6.wireOp",EDGE,"E68.trimOffspring")])]});
            var Q18;
            Q18=makeQuery(id+"F7.opExtrude","SWEPT_EDGE",EDGE,{"disambiguationData":[OSD([sQuery(id+"F6.wireOp",EDGE,"E62.8.0.0"),sQuery(id+"F6.wireOp",EDGE,"E75.trimOffspring")])]});
            var Q19;
            Q19=makeQuery(id+"F7.opExtrude","SWEPT_EDGE",EDGE,{"disambiguationData":[OSD([sQuery(id+"F6.wireOp",EDGE,"E62.7.0.1"),sQuery(id+"F6.wireOp",EDGE,"E75.trimOffspring")])]});
            var Q20;
            Q20=makeQuery(id+"F7.opExtrude","SWEPT_EDGE",EDGE,{"disambiguationData":[OSD([sQuery(id+"F6.wireOp",EDGE,"E62.7.0.0"),sQuery(id+"F6.wireOp",EDGE,"E74.trimOffspring")])]});
            var Q21;
            Q21=makeQuery(id+"F7.opExtrude","SWEPT_EDGE",EDGE,{"disambiguationData":[OSD([sQuery(id+"F6.wireOp",EDGE,"E62.6.0.1"),sQuery(id+"F6.wireOp",EDGE,"E74.trimOffspring")])]});
            var Q22;
            Q22=makeQuery(id+"F7.opExtrude","SWEPT_EDGE",EDGE,{"disambiguationData":[OSD([sQuery(id+"F6.wireOp",EDGE,"E62.5.0.1"),sQuery(id+"F6.wireOp",EDGE,"E73.trimOffspring")])]});
            var Q23;
            Q23=makeQuery(id+"F7.opExtrude","SWEPT_EDGE",EDGE,{"disambiguationData":[OSD([sQuery(id+"F6.wireOp",EDGE,"E65.trimOffspring"),sQuery(id+"F6.wireOp",EDGE,"E86.MirrorCS")])]});
            var Q24;
            Q24=makeQuery(id+"F7.opExtrude","SWEPT_EDGE",EDGE,{"disambiguationData":[OSD([sQuery(id+"F6.wireOp",EDGE,"E62.3.0.1"),sQuery(id+"F6.wireOp",EDGE,"3dc599b9-d0b6-47b3-8b11-184a39de6bda2.MirrorCS")])]});
            var Q25;
            Q25=makeQuery(id+"F7.opExtrude","SWEPT_EDGE",EDGE,{"disambiguationData":[OSD([sQuery(id+"F6.wireOp",EDGE,"E62.2.0.1"),sQuery(id+"F6.wireOp",EDGE,"E87.MirrorCS")])]});
            var Q26;
            Q26=makeQuery(id+"F7.opExtrude","SWEPT_EDGE",EDGE,{"disambiguationData":[OSD([sQuery(id+"F6.wireOp",EDGE,"E62.1.0.1"),sQuery(id+"F6.wireOp",EDGE,"E71.trimOffspring")])]});
            var Q27;
            Q27=makeQuery(id+"F7.opExtrude","SWEPT_EDGE",EDGE,{"disambiguationData":[OSD([sQuery(id+"F6.wireOp",EDGE,"E61"),sQuery(id+"F6.wireOp",EDGE,"E70.trimOffspring")])]});
            var Q28;
            Q28=makeQuery(id+"F7.opExtrude","SWEPT_EDGE",EDGE,{"disambiguationData":[OSD([sQuery(id+"F6.wireOp",EDGE,"E58"),sQuery(id+"F6.wireOp",EDGE,"E59")])]});
            var Q29;
            Q29=makeQuery(id+"F7.opExtrude","SWEPT_EDGE",EDGE,{"disambiguationData":[OSD([sQuery(id+"F6.wireOp",EDGE,"E62.6.0.0"),sQuery(id+"F6.wireOp",EDGE,"E73.trimOffspring")])]});
            var Q30;
            Q30=makeQuery(id+"F7.opExtrude","SWEPT_EDGE",EDGE,{"disambiguationData":[OSD([sQuery(id+"F6.wireOp",EDGE,"E62.5.0.0"),sQuery(id+"F6.wireOp",EDGE,"E86.MirrorCS")])]});
            var Q31;
            Q31=makeQuery(id+"F7.opExtrude","SWEPT_EDGE",EDGE,{"disambiguationData":[OSD([sQuery(id+"F6.wireOp",EDGE,"189e8fec-66c5-48d0-8221-c3fc3ef3f735.trimOffspring"),sQuery(id+"F6.wireOp",EDGE,"3dc599b9-d0b6-47b3-8b11-184a39de6bda2.MirrorCS")])]});
            var Q32;
            Q32=makeQuery(id+"F7.opExtrude","SWEPT_EDGE",EDGE,{"disambiguationData":[OSD([sQuery(id+"F6.wireOp",EDGE,"E62.3.0.0"),sQuery(id+"F6.wireOp",EDGE,"E87.MirrorCS")])]});
            var Q33;
            Q33=makeQuery(id+"F7.opExtrude","SWEPT_EDGE",EDGE,{"disambiguationData":[OSD([sQuery(id+"F6.wireOp",EDGE,"E62.2.0.0"),sQuery(id+"F6.wireOp",EDGE,"E71.trimOffspring")])]});
            var Q34;
            Q34=makeQuery(id+"F7.opExtrude","SWEPT_EDGE",EDGE,{"disambiguationData":[OSD([sQuery(id+"F6.wireOp",EDGE,"E62.1.0.0"),sQuery(id+"F6.wireOp",EDGE,"E70.trimOffspring")])]});
            var Q35;
            Q35=makeQuery(id+"F7.opExtrude","SWEPT_EDGE",EDGE,{"disambiguationData":[OSD([sQuery(id+"F6.wireOp",EDGE,"E59"),sQuery(id+"F6.wireOp",EDGE,"E60")])]});
            fillet(context, id + "F9", {"entities" : qUnion([Q0, Q1, Q2, Q3, Q4, Q5, Q6, Q7, Q8, Q9, Q10, Q11, Q12, Q13, Q14, Q15, Q16, Q17, Q18, Q19, Q20, Q21, Q22, Q23, Q24, Q25, Q26, Q27, Q28, Q29, Q30, Q31, Q32, Q33, Q34, Q35]), "tangentPropagation" : true, "radius" : 2 * mm, "defaultsChanged" : true, "vertexSettings" : [], "allowEdgeOverflow" : false});
        }
        {
            var Q0;
            Q0=makeQuery(id+"F7.opExtrude","SWEPT_EDGE",EDGE,{"disambiguationData":[OSD([sQuery(id+"F6.wireOp",EDGE,"E72.trimOffspring"),sQuery(id+"F6.wireOp",EDGE,"E82.MirrorCS")])]});
            var Q1;
            Q1=makeQuery(id+"F7.opExtrude","SWEPT_EDGE",EDGE,{"disambiguationData":[OSD([sQuery(id+"F6.wireOp",EDGE,"E72.trimOffspring"),sQuery(id+"F6.wireOp",EDGE,"E84.MirrorCS")])]});
            var Q2;
            Q2=makeQuery(id+"F7.opExtrude","SWEPT_EDGE",EDGE,{"disambiguationData":[OSD([sQuery(id+"F6.wireOp",EDGE,"E82.MirrorCS"),sQuery(id+"F6.wireOp",EDGE,"E83.MirrorCS")])]});
            var Q3;
            Q3=makeQuery(id+"F7.opExtrude","SWEPT_EDGE",EDGE,{"disambiguationData":[OSD([sQuery(id+"F6.wireOp",EDGE,"E83.MirrorCS"),sQuery(id+"F6.wireOp",EDGE,"E84.MirrorCS")])]});
            var Q4;
            Q4=makeQuery(id+"F7.opExtrude","SWEPT_EDGE",EDGE,{"disambiguationData":[OSD([sQuery(id+"F6.wireOp",EDGE,"E56.2"),sQuery(id+"F6.wireOp",EDGE,"E56.5")])]});
            var Q5;
            Q5=makeQuery(id+"F7.opExtrude","SWEPT_EDGE",EDGE,{"disambiguationData":[OSD([sQuery(id+"F6.wireOp",EDGE,"E56.2"),sQuery(id+"F6.wireOp",EDGE,"E56.7")])]});
            var Q6;
            Q6=makeQuery(id+"F7.opExtrude","SWEPT_EDGE",EDGE,{"disambiguationData":[OSD([sQuery(id+"F6.wireOp",EDGE,"E56.6"),sQuery(id+"F6.wireOp",EDGE,"E56.7")])]});
            var Q7;
            Q7=makeQuery(id+"F7.opExtrude","SWEPT_EDGE",EDGE,{"disambiguationData":[OSD([sQuery(id+"F6.wireOp",EDGE,"E56.5"),sQuery(id+"F6.wireOp",EDGE,"E56.6")])]});
            fillet(context, id + "F10", {"entities" : qUnion([Q0, Q1, Q2, Q3, Q4, Q5, Q6, Q7]), "tangentPropagation" : true, "radius" : .5 * mm, "defaultsChanged" : false, "vertexSettings" : [], "allowEdgeOverflow" : false});
        }
    });
